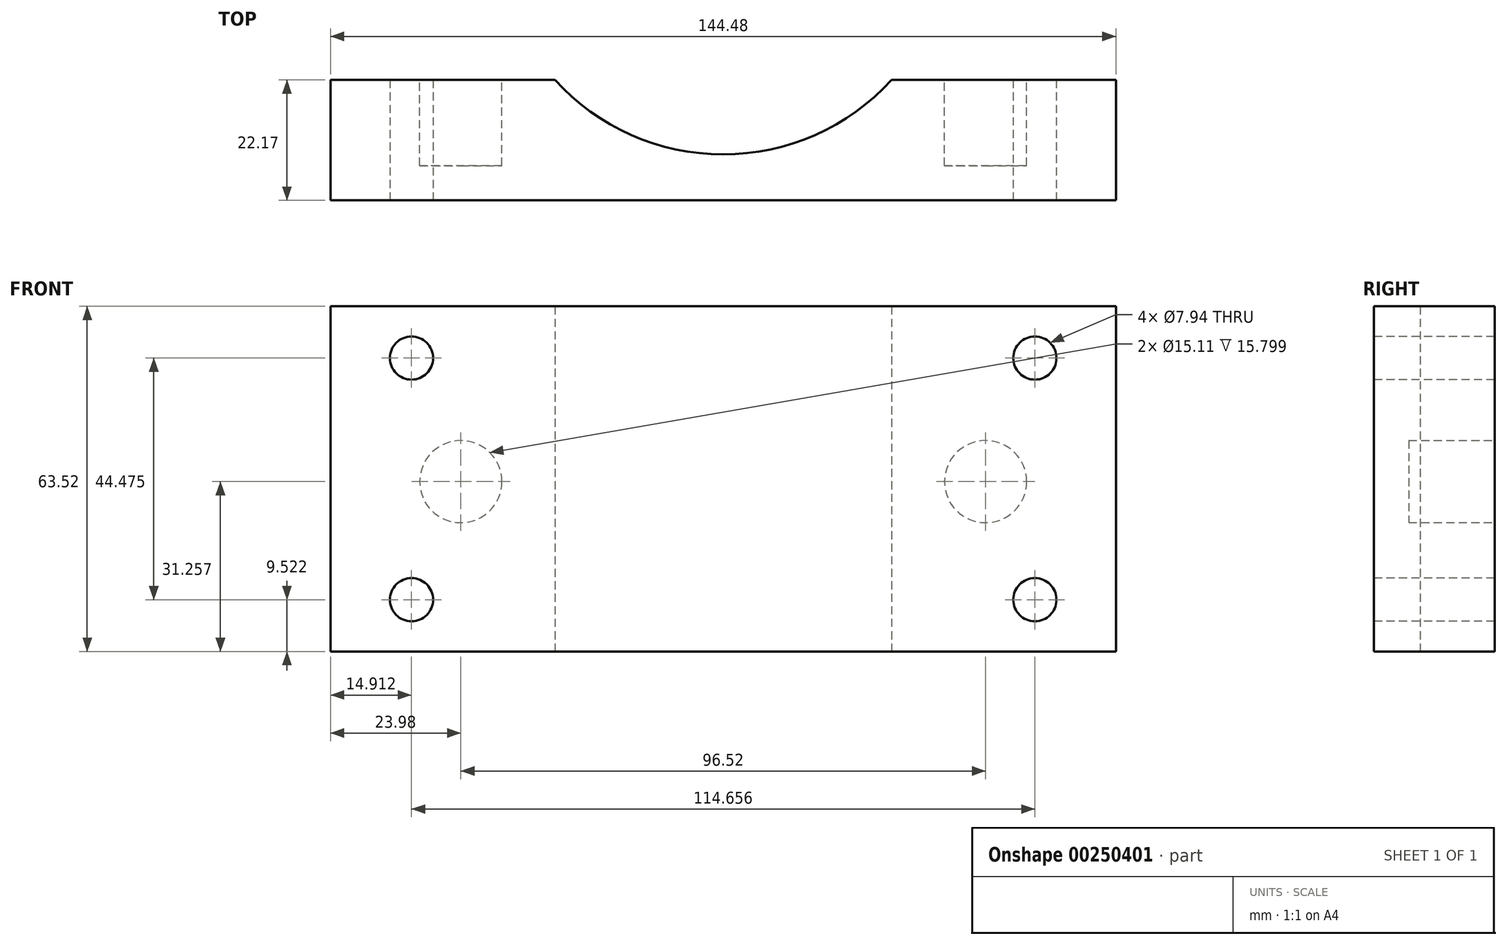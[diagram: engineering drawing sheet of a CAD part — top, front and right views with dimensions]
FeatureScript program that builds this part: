
annotation { "Feature Type Name" : "Feature", "Feature Type Description" : "" }
export const myFeature = defineFeature(function(context is Context, id is Id, definition is map)
    precondition{}
    {
        {
            var Q0;
            Q0=qCreatedBy(makeId("Front.planeOp"),FACE);
            var sketch = newSketch(context, id + "F0", { "sketchPlane" : qUnion([Q0])});
            skLineSegment(sketch, "E0.bottom", {"start": v(72.24, -31.76) * mm, "end": v(-72.24, -31.76) * mm});
            skLineSegment(sketch, "E0.top", {"start": v(72.24, 31.76) * mm, "end": v(-72.24, 31.76) * mm});
            skLineSegment(sketch, "E0.left", {"start": v(72.24, -31.76) * mm, "end": v(72.24, 31.76) * mm});
            skLineSegment(sketch, "E0.right", {"start": v(-72.24, -31.76) * mm, "end": v(-72.24, 31.76) * mm});
            skPoint(sketch, "E0.middle", {"position": v(0, 0) * mm});
            skSolve(sketch);
        }
        {
            var Q0;
            Q0=makeQuery(id+"F0.imprint","IMPRINT",FACE,{"disambiguationData":[TD([[makeQuery(id+"F0.imprint","IMPRINT",EDGE,{"derivedFrom":sQuery(id+"F0.wireOp",EDGE,"E0.bottom")}),-1.0]])]});
            extrude(context, id + "F1", {"entities" : qUnion([Q0]), "depth" : 22.17 * mm});
        }
        {
            var Q0;
            Q0=makeQuery(id+"F1.opExtrude","CAP_FACE",FACE,{"disambiguationData":[OSD([sQuery(id+"F0.wireOp",EDGE,"E0.bottom"),sQuery(id+"F0.wireOp",EDGE,"E0.top"),sQuery(id+"F0.wireOp",EDGE,"E0.left"),sQuery(id+"F0.wireOp",EDGE,"E0.right")])],"isStart":false});
            var sketch = newSketch(context, id + "F2", { "sketchPlane" : qUnion([Q0])});
            skCircle(sketch, "E1", {"center": v(-57.33, 22.24) * mm, "radius": 3.97 * mm});
            skCircle(sketch, "E2", {"center": v(-57.33, -22.24) * mm, "radius": 3.97 * mm});
            skCircle(sketch, "E3", {"center": v(57.33, 22.24) * mm, "radius": 3.97 * mm});
            skCircle(sketch, "E4", {"center": v(57.33, -22.24) * mm, "radius": 3.97 * mm});
            skSolve(sketch);
        }
        {
            var Q0;
            Q0=makeQuery(id+"F2.imprint","IMPRINT",FACE,{"disambiguationData":[TD([[makeQuery(id+"F2.imprint","IMPRINT",EDGE,{"derivedFrom":sQuery(id+"F2.wireOp",EDGE,"E1")}),1.0]])]});
            var Q1;
            Q1=makeQuery(id+"F2.imprint","IMPRINT",FACE,{"disambiguationData":[TD([[makeQuery(id+"F2.imprint","IMPRINT",EDGE,{"derivedFrom":sQuery(id+"F2.wireOp",EDGE,"E2")}),1.0]])]});
            var Q2;
            Q2=makeQuery(id+"F2.imprint","IMPRINT",FACE,{"disambiguationData":[TD([[makeQuery(id+"F2.imprint","IMPRINT",EDGE,{"derivedFrom":sQuery(id+"F2.wireOp",EDGE,"E4")}),1.0]])]});
            var Q3;
            Q3=makeQuery(id+"F2.imprint","IMPRINT",FACE,{"disambiguationData":[TD([[makeQuery(id+"F2.imprint","IMPRINT",EDGE,{"derivedFrom":sQuery(id+"F2.wireOp",EDGE,"E3")}),1.0]])]});
            extrude(context, id + "F3", {"entities" : qUnion([Q0, Q1, Q2, Q3]), "operationType" : NewBodyOperationType.REMOVE, "endBound" : BoundingType.THROUGH_ALL, "oppositeDirection" : true, "depth" : 25.4 * mm});
        }
        {
            var Q0;
            Q0=makeQuery(id+"F1.opExtrude","SWEPT_FACE",FACE,{"disambiguationData":[OSD([sQuery(id+"F0.wireOp",EDGE,"E0.bottom")])]});
            var sketch = newSketch(context, id + "F4", { "sketchPlane" : qUnion([Q0])});
            skLineSegment(sketch, "E5", {"start": v(0, 22.17) * mm, "end": v(0, 13.72) * mm});
            skPoint(sketch, "E5.endSnap0", {"position": v(0, 22.17) * mm});
            skLineSegment(sketch, "E6", {"start": v(-72.24, 0) * mm, "end": v(-30.96, 0) * mm});
            skLineSegment(sketch, "E7", {"start": v(72.24, 0) * mm, "end": v(30.96, 0) * mm});
            skArc(sketch, "E8", {"start": v(30.96, 0) * mm, "mid": v(0, 13.72) * mm, "end": v(-30.96, 0) * mm});
            skSolve(sketch);
        }
        {
            var Q0;
            {var subQ0=sQuery(id+"F4.wireOp",EDGE,"E8");var subQ1=makeQuery(id+"F4.imprint","INTERSECT",VERTEX,{"derivedFrom":[sQuery(id+"F4.wireOp",EDGE,"E5"),subQ0]});Q0=makeQuery(id+"F4.imprint","IMPRINT",FACE,{"disambiguationData":[TD([[makeQuery(id+"F4.imprint","IMPRINT",EDGE,{"disambiguationData":[TD([[subQ1,1.0]])],"derivedFrom":subQ0}),1.0]])]});}
            extrude(context, id + "F5", {"entities" : qUnion([Q0]), "operationType" : NewBodyOperationType.REMOVE, "endBound" : BoundingType.THROUGH_ALL, "oppositeDirection" : true, "depth" : 25.4 * mm});
        }
        {
            var Q0;
            {var subQ0=sQuery(id+"F0.wireOp",EDGE,"E0.top");var subQ1=sQuery(id+"F0.wireOp",EDGE,"E0.left");var subQ2=sQuery(id+"F0.wireOp",EDGE,"E0.bottom");Q0=makeQuery(id+"F5.boolean.opBoolean","SPLIT",FACE,{"disambiguationData":[TD([makeQuery(id+"F1.opExtrude","SWEPT_FACE",FACE,{"disambiguationData":[OSD([subQ1])]})])],"derivedFrom":makeQuery(id+"F1.opExtrude","CAP_FACE",FACE,{"disambiguationData":[OSD([subQ2,subQ0,subQ1,sQuery(id+"F0.wireOp",EDGE,"E0.right")])],"isStart":true})});}
            var sketch = newSketch(context, id + "F6", { "sketchPlane" : qUnion([Q0])});
            skLineSegment(sketch, "E9", {"start": v(-30.96, 0) * mm, "end": v(-48.26, 0) * mm});
            skLineSegment(sketch, "E10", {"start": v(-48.26, 0) * mm, "end": v(-48.26, -0.5) * mm});
            skCircle(sketch, "E11", {"center": v(-48.26, -0.5) * mm, "radius": 7.56 * mm});
            skSolve(sketch);
        }
        {
            var Q0;
            Q0=makeQuery(id+"F6.imprint","IMPRINT",FACE,{"disambiguationData":[TD([[makeQuery(id+"F6.imprint","IMPRINT",EDGE,{"derivedFrom":sQuery(id+"F6.wireOp",EDGE,"E11")}),1.0]])]});
            extrude(context, id + "F7", {"entities" : qUnion([Q0]), "operationType" : NewBodyOperationType.REMOVE, "oppositeDirection" : true, "depth" : 15.8 * mm});
        }
        {
            var Q0;
            {var subQ0=sQuery(id+"F0.wireOp",EDGE,"E0.right");var subQ1=sQuery(id+"F0.wireOp",EDGE,"E0.top");var subQ2=sQuery(id+"F0.wireOp",EDGE,"E0.bottom");Q0=makeQuery(id+"F5.boolean.opBoolean","SPLIT",FACE,{"disambiguationData":[TD([makeQuery(id+"F1.opExtrude","SWEPT_FACE",FACE,{"disambiguationData":[OSD([subQ0])]})])],"derivedFrom":makeQuery(id+"F1.opExtrude","CAP_FACE",FACE,{"disambiguationData":[OSD([subQ2,subQ1,sQuery(id+"F0.wireOp",EDGE,"E0.left"),subQ0])],"isStart":true})});}
            var sketch = newSketch(context, id + "F8", { "sketchPlane" : qUnion([Q0])});
            skLineSegment(sketch, "E12", {"start": v(30.96, 0) * mm, "end": v(48.26, 0) * mm});
            skLineSegment(sketch, "E13", {"start": v(48.26, 0) * mm, "end": v(48.26, -0.5) * mm});
            skCircle(sketch, "E14", {"center": v(48.26, -0.5) * mm, "radius": 7.56 * mm});
            skSolve(sketch);
        }
        {
            var Q0;
            Q0=makeQuery(id+"F8.imprint","IMPRINT",FACE,{"disambiguationData":[TD([[makeQuery(id+"F8.imprint","IMPRINT",EDGE,{"derivedFrom":sQuery(id+"F8.wireOp",EDGE,"E14")}),1.0]])]});
            extrude(context, id + "F9", {"entities" : qUnion([Q0]), "operationType" : NewBodyOperationType.REMOVE, "oppositeDirection" : true, "depth" : 15.8 * mm});
        }
    });
